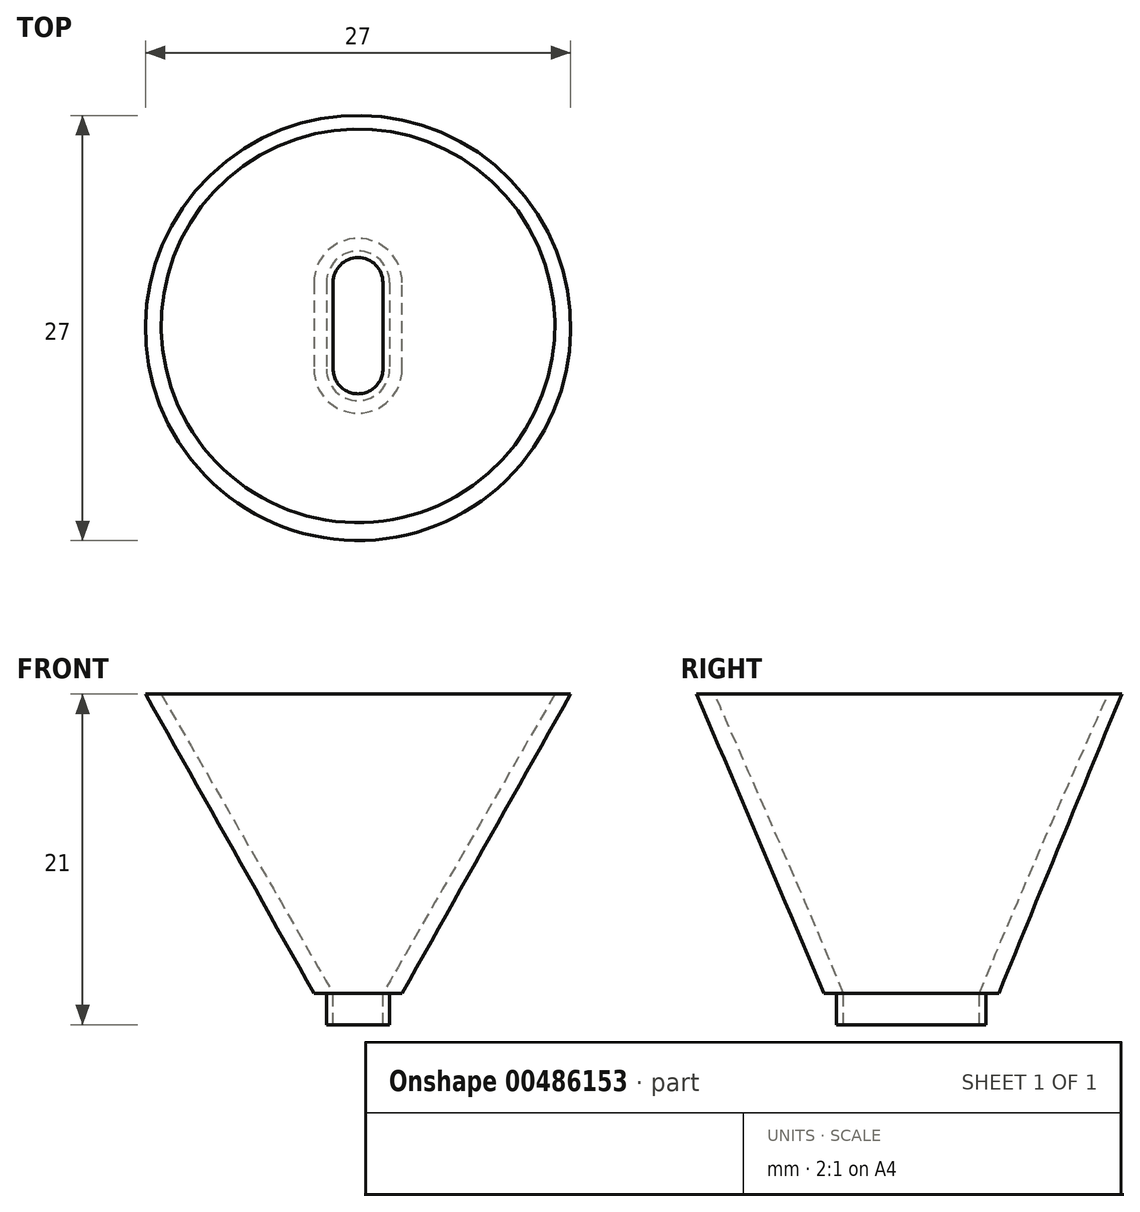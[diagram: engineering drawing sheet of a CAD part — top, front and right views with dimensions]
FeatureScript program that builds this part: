
annotation { "Feature Type Name" : "Feature", "Feature Type Description" : "" }
export const myFeature = defineFeature(function(context is Context, id is Id, definition is map)
    precondition{}
    {
        {
            var Q0;
            Q0=qCreatedBy(makeId("Top.planeOp"),FACE);
            var sketch = newSketch(context, id + "F0", { "sketchPlane" : qUnion([Q0])});
            skLineSegment(sketch, "E0", {"start": v(-2, 0) * mm, "end": v(-2, -5.5) * mm});
            skLineSegment(sketch, "E1", {"start": v(2, 0) * mm, "end": v(2, -5.5) * mm});
            skArc(sketch, "E2", {"start": v(-2, -5.5) * mm, "mid": v(0, -7.5) * mm, "end": v(2, -5.5) * mm});
            skArc(sketch, "E3", {"start": v(2, 0) * mm, "mid": v(0, 2) * mm, "end": v(-2, 0) * mm});
            skSolve(sketch);
        }
        {
            var Q0;
            Q0=qCreatedBy(makeId("Top.planeOp"),FACE);
            var sketch = newSketch(context, id + "F1", { "sketchPlane" : qUnion([Q0])});
            skLineSegment(sketch, "E4", {"start": v(-1.58, 0) * mm, "end": v(-1.58, -5.48) * mm});
            skLineSegment(sketch, "E5", {"start": v(1.58, -5.5) * mm, "end": v(1.58, 0) * mm});
            skArc(sketch, "E6", {"start": v(1.58, 0) * mm, "mid": v(0, 1.58) * mm, "end": v(-1.58, 0) * mm});
            skArc(sketch, "E7", {"start": v(-1.58, -5.48) * mm, "mid": v(0, -7.07) * mm, "end": v(1.58, -5.5) * mm});
            skSolve(sketch);
        }
        {
            var Q0;
            Q0=qCreatedBy(makeId("Top.planeOp"),FACE);
            var sketch = newSketch(context, id + "F2", { "sketchPlane" : qUnion([Q0])});
            skLineSegment(sketch, "E8", {"start": v(-2.8, 0) * mm, "end": v(-2.8, -5.5) * mm});
            skLineSegment(sketch, "E9", {"start": v(-2.8, -5.5) * mm, "end": v(2.8, -5.5) * mm});
            skLineSegment(sketch, "E10", {"start": v(2.8, -5.5) * mm, "end": v(2.8, 0) * mm});
            skArc(sketch, "E11", {"start": v(2.8, 0) * mm, "mid": v(0, 2.8) * mm, "end": v(-2.8, 0) * mm});
            skArc(sketch, "E12", {"start": v(-2.8, -5.5) * mm, "mid": v(0, -8.3) * mm, "end": v(2.8, -5.5) * mm});
            skSolve(sketch);
        }
        {
            var Q0;
            Q0=qCreatedBy(makeId("Top.planeOp"),FACE);
            cPlane(context, id + "F3", {"entities" : qUnion([Q0]), "cplaneType" : CPlaneType.OFFSET, "offset" : 19 * mm, "width" : 150 * mm, "height" : 150 * mm});
        }
        {
            var Q0;
            Q0=qCreatedBy(id+"F3.planeOp",FACE);
            var sketch = newSketch(context, id + "F4", { "sketchPlane" : qUnion([Q0])});
            skCircle(sketch, "E13", {"center": v(0, -2.75) * mm, "radius": 12.5 * mm});
            skSolve(sketch);
        }
        {
            var Q0;
            Q0=qCreatedBy(id+"F3.planeOp",FACE);
            var sketch = newSketch(context, id + "F5", { "sketchPlane" : qUnion([Q0])});
            skCircle(sketch, "E14", {"center": v(0, -2.9) * mm, "radius": 13.5 * mm});
            skSolve(sketch);
        }
        {
            var Q0;
            Q0 = qSketchRegion(id + "F2", true);
            var Q1;
            Q1 = qSketchRegion(id + "F5", true);
            loft(context, id + "F6", {"sheetProfilesArray" : [{ "sheetProfileEntities" : qUnion([Q0]) }, { "sheetProfileEntities" : qUnion([Q1]) }]});
        }
        {
            var Q1;
            Q1 = qSketchRegion(id + "F4", true);
            var Q2;
            Q2 = qSketchRegion(id + "F1", true);
            loft(context, id + "F7", {"operationType" : NewBodyOperationType.REMOVE, "sheetProfilesArray" : [{ "sheetProfileEntities" : qUnion([Q1]) }, { "sheetProfileEntities" : qUnion([Q2]) }]});
        }
        {
            var Q0;
            Q0=makeQuery(id+"F0.imprint","IMPRINT",FACE,{"disambiguationData":[TD([[makeQuery(id+"F0.imprint","IMPRINT",EDGE,{"derivedFrom":sQuery(id+"F0.wireOp",EDGE,"E0")}),1.0]])]});
            extrude(context, id + "F8", {"entities" : qUnion([Q0]), "operationType" : NewBodyOperationType.ADD, "oppositeDirection" : true, "depth" : 2 * mm, "offsetDistance" : 25 * mm});
        }
        {
            var Q0;
            Q0 = qSketchRegion(id + "F1", true);
            extrude(context, id + "F9", {"entities" : qUnion([Q0]), "operationType" : NewBodyOperationType.REMOVE, "oppositeDirection" : true, "depth" : 2 * mm, "offsetDistance" : 25 * mm});
        }
    });
